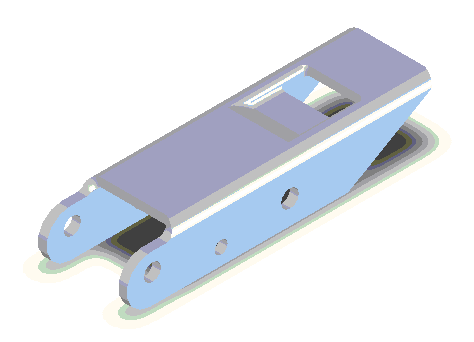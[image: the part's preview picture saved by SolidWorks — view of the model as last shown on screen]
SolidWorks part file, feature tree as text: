
SOLIDWORKS PART (.sldprt)
format: sldprt  version: not decoded by parser v0  size: 265,728 bytes
history: native  units: mm
features: sketch x8, fillet x5, cut_extrude x3, extrude x1, shell x1, sheet_metal_op x1 + 1 further entry (+11 scaffold rows collapsed)
feature tree (31):
  scaffold x11  (default folders/planes/origin — collapsed)
  sketch  "Sketch1"  dims[D1=11.0mm D2=~59.968722mm]
  extrude  "Extrude1"  Depth=16.4mm
  sketch  "Sketch2"  dims[c1.D3=2.0mm c1.D10=1.0mm c1.D11=3.3mm c1.D12=2.4mm c1.D13=3.2mm c1.D14=3.2mm c1.D15=3.2mm c1.D16=3.2mm c1.D17=3.2mm c1.D18=3.2mm c1.D19=3.3mm c1.D1=9.5mm c1.D2=2.3mm c1.D4=19.1mm c1.D5=~6.813916mm c1.D6=8.0mm c1.D7=3.0mm c2.D5=5.0mm c2.D8=1.7mm c2.D9=1.0mm c2.D13=17.4625mm c2.D14=12.7mm c2.D16=4.7625mm c2.D17=5.334mm c2.D18=2.97mm c2.D19=4.42mm c2.D20=56.5mm c3.D5=~20.600918mm c4.D5=30.0deg]
  cut_extrude  "Cut-Extrude2"  Depth=16.4mm
  sketch  "Sketch3"  dims[D3=2.3mm D1=9.5mm D2=2.3mm]
  cut_extrude  "Cut-Extrude3"  [1 undecoded]
  fillet  "Fillet1"  [1 undecoded]
  sketch  "Sketch4"  dims[c1.D1=10.0mm c1.D2=~9.198407mm c2.D2=90.0deg c3.D2=29.0mm c3.D3=12.8mm]
  cut_extrude  "Cut-Extrude4"  [1 undecoded]
  shell  "Shell15"  Thickness=1.6mm
  sheet_metal_op  "Sheet-Metal2"  Thickness=1.6mm
  sketch  "Sharp-Sketch2"  dims[c1.SharpBend1=0.0 c1.D1=0.0mm c1.D4=90.0deg c1.D5=2.0 c1.D8=0.0mm c1.D9=0.0mm c2.D1=0.5mm c2.D2=500.0mm c2.D3=0.0mm c2.D4=90.0deg c2.D5=1.0 c2.D8=0.0mm c2.D9=0.0mm]
  sketch  "Flat-Sketch2"  dims[D1=0.5mm D2=500.0mm D3=0.0mm]
  sketch  "Sketch5"  dims[c1.D1=8.0mm c1.D2=~3.201314mm c2.D2=35.0deg c2.D1=10.5mm c2.D5=1.6mm c2.D6=1.0mm c2.D7=5.0mm]
  fillet  "Fillet2"  Radius=5mm
  fillet  "Fillet3"  Radius=0.75mm
  fillet  "Fillet4"  Radius=0.75mm
  fillet  "Fillet5"  Radius=0.75mm
  "Flat-Pattern1"
  sketch  "Bend-Lines1"
decode coverage: 15 of 19 modeling features carry decoded parameters; 1 rows unclassified (native names shown)
note: ~ marks probable driven/reference dimensions
note: 3 parameter values undecoded
summary: no parameter record found for 3 features
note: suppression state not decoded; provenance and decode notes live in map.json
